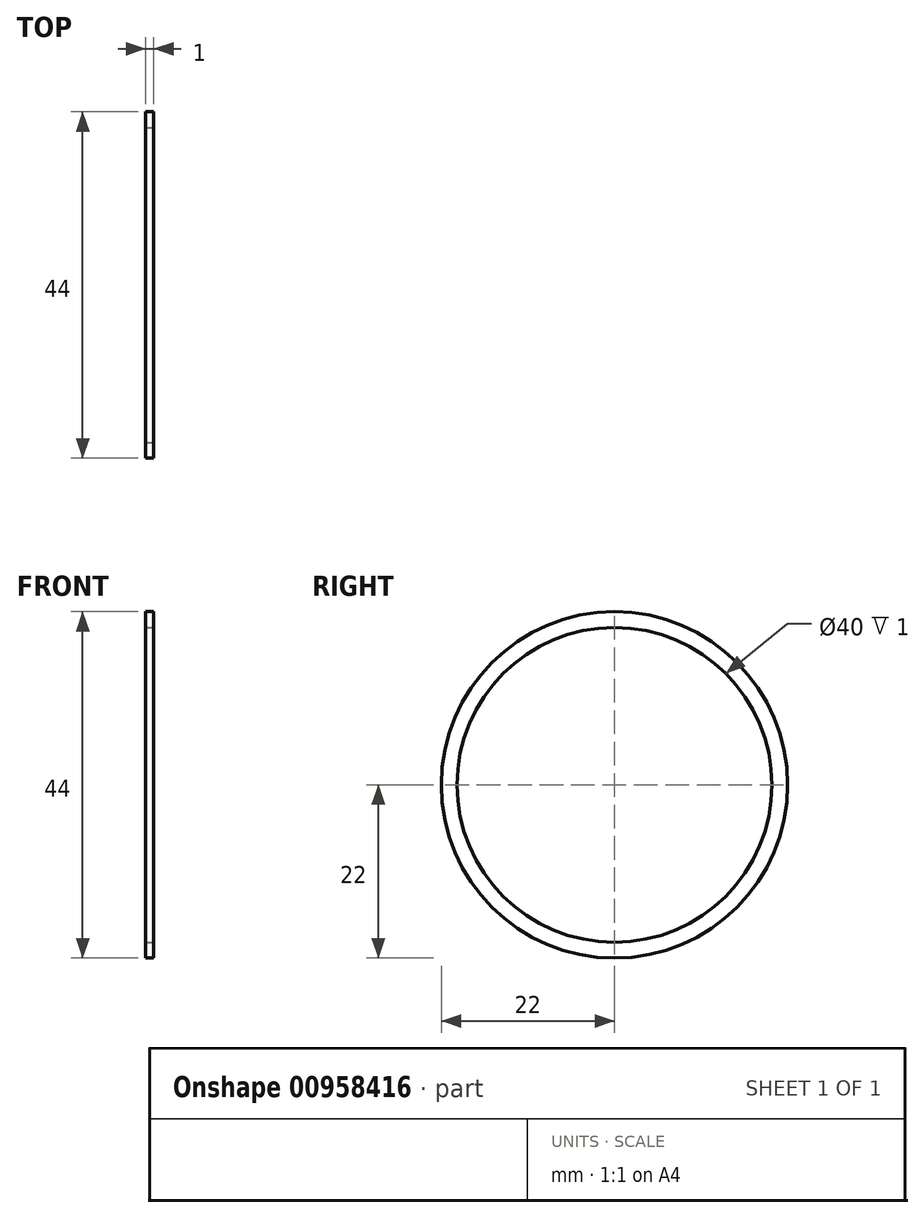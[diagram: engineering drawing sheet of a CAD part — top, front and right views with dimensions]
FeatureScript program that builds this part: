
annotation { "Feature Type Name" : "Feature", "Feature Type Description" : "" }
export const myFeature = defineFeature(function(context is Context, id is Id, definition is map)
    precondition{}
    {
        {
            var Q0;
            Q0=qCreatedBy(makeId("Front.planeOp"),FACE);
            var sketch = newSketch(context, id + "F0", { "sketchPlane" : qUnion([Q0])});
            skLineSegment(sketch, "E0.bottom", {"start": v(-14.02, 22) * mm, "end": v(-15.02, 22) * mm});
            skLineSegment(sketch, "E0.top", {"start": v(-14.02, 20) * mm, "end": v(-15.02, 20) * mm});
            skLineSegment(sketch, "E0.left", {"start": v(-14.02, 22) * mm, "end": v(-14.02, 20) * mm});
            skLineSegment(sketch, "E0.right", {"start": v(-15.02, 22) * mm, "end": v(-15.02, 20) * mm});
            skLineSegment(sketch, "E1", {"start": v(0, 0) * mm, "end": v(-14.12, 0) * mm});
            skSolve(sketch);
        }
        {
            var Q0;
            Q0=qSketchRegion(id+"F0",true);
            var Q1;
            Q1=sQuery(id+"F0.wireOp",EDGE,"E1");
            revolve(context, id + "F1", {"surfaceOperationType" : NewSurfaceOperationType.NEW, "entities" : qUnion([Q0]), "axis" : qUnion([Q1]), "revolveType" : RevolveType.FULL});
        }
    });
